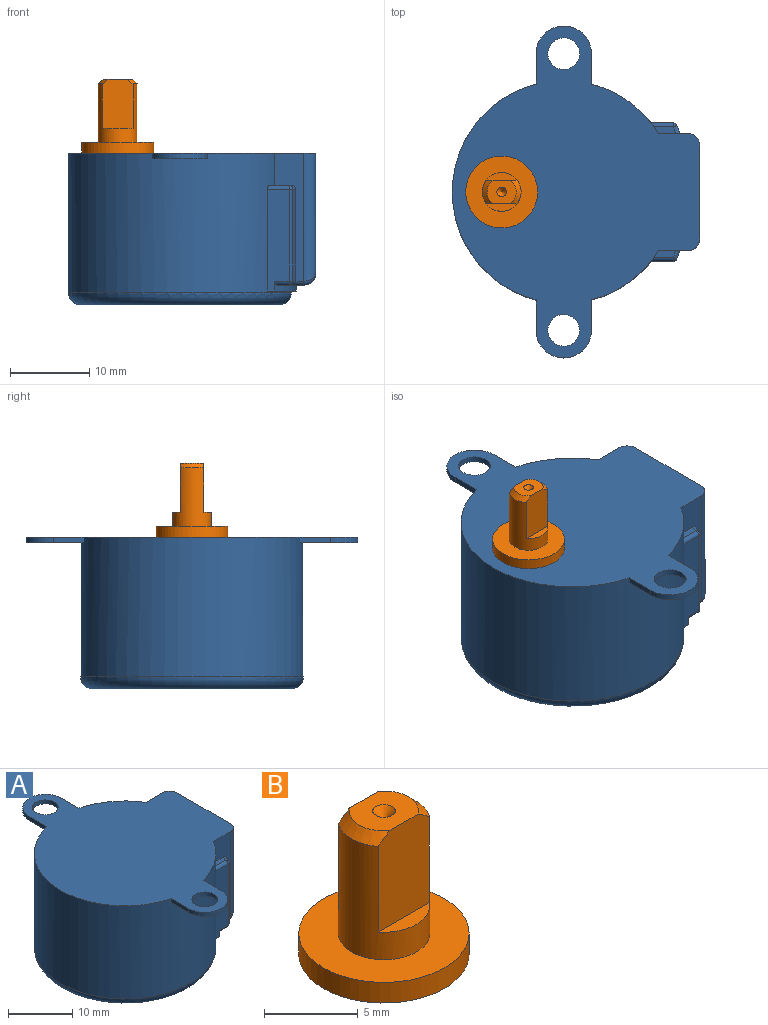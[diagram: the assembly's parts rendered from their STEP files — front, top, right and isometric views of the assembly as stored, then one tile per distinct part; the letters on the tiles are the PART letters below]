
ASSEMBLY  parts=2 mates=1
PART A: 53 faces, bbox 32.5x42x19.2 mm
  f0: plane 15.2x11.8mm, normal (1,0,0), area 169.8mm2, adj f14,f26,f27,f28,f48,f49,f50,f51
  f1: cylinder r=14.1mm len=28.2mm, axis (0,0,1), area 1250mm2, adj f2,f3,f4,f5,f6,f7,f8,f13
  f2: plane 16.5x4.27mm, normal (0,0,-1), area 30.7mm2, adj f1,f23,f24,f27,f34,f36,f37,f42
  f3: plane 16.2x3.7mm, normal (0,1,0), area 27.3mm2, adj f1,f14,f17,f18,f26,f30,f37
  f4: plane 3.84x0.75mm, normal (-1,0,0), area 2.9mm2, adj f1,f10,f13,f14
  f5: plane 3.84x0.75mm, normal (-1,0,0), area 2.9mm2, adj f1,f8,f9,f14
  f6: plane 3.84x0.75mm, normal (1,0,0), area 2.9mm2, adj f1,f10,f13,f14
  f7: plane 3.84x0.75mm, normal (1,0,0), area 2.9mm2, adj f1,f8,f9,f14
  f8: plane 7.34x7mm, normal (0,0,-1), area 31.5mm2, adj f1,f5,f7,f9,f12
  f9: cylinder r=3.5mm len=7mm, axis (0,0,1), area 8.2mm2, adj f5,f7,f8,f14
  f10: cylinder r=3.5mm len=7mm, axis (0,0,1), area 8.2mm2, adj f4,f6,f13,f14
  f11: cylinder r=2mm len=4mm, axis (0,0,1), area 9.4mm2, adj f13,f14
  f12: cylinder r=2mm len=4mm, axis (0,0,1), area 9.4mm2, adj f8,f14
  f13: plane 7.34x7mm, normal (0,0,-1), area 31.5mm2, adj f1,f4,f6,f10,f11
  f14: plane 42x31.3mm, normal (0,0,1), area 742.5mm2, adj f0,f1,f3,f4,f5,f6,f7,f9
  f15: plane 25.2x25.2mm, normal (0,0,-1), area 498.8mm2, adj f29
  f16: plane 16.2x3.7mm, normal (0,-1,0), area 27.3mm2, adj f1,f14,f20,f21,f28,f40,f46
  f17: plane 2.73x0.85mm, normal (0,0,1), area 1.9mm2, adj f1,f3,f30,f31
  f18: plane 11.6x1.02mm, normal (0.94,0.35,0), area 12.7mm2, adj f3,f30,f33,f36
  f19: plane 11.6x2.8mm, normal (0,1,0), area 32.4mm2, adj f1,f31,f33,f34
  f20: plane 2.73x0.85mm, normal (0,0,1), area 1.9mm2, adj f1,f16,f39,f40
  f21: plane 11.6x1.02mm, normal (0.94,-0.35,0), area 12.7mm2, adj f16,f40,f43,f45
  f22: plane 12.85x2.8mm, normal (0,-1,0), area 33.6mm2, adj f1,f23,f25,f39,f42,f43
  f23: cylinder r=14.85mm len=7.25mm, axis (0,0,1), area 6mm2, adj f2,f22,f24,f25,f42
  f24: plane 0.75x0.75mm, normal (0,1,0), area 0.6mm2, adj f1,f2,f23,f25
  f25: plane 7.25x3.71mm, normal (0,0,-1), area 5.9mm2, adj f1,f22,f23,f24
  f26: cylinder r=1.5mm len=16.2mm, axis (0,0,-1), area 37.3mm2, adj f0,f3,f14,f38
  f27: cylinder r=1.5mm len=13.8mm, axis (0,-1,0), area 30.8mm2, adj f0,f2,f38,f47
  f28: cylinder r=1.5mm len=16.2mm, axis (0,0,1), area 37.3mm2, adj f0,f14,f16,f47
  f29: torus R=12.6mm, axis (0,0,-1), area 200.7mm2, adj f1,f15
  f30: cylinder r=0.5mm len=1.2mm, axis (-0.35,0.94,0), area 0.8mm2, adj f3,f17,f18,f32
  f31: cylinder r=0.5mm len=2.8mm, axis (-1,0,0), area 2.1mm2, adj f1,f17,f19,f32
  f32: sphere r=0.5mm, area 0.3mm2, adj f30,f31,f33
  f33: cylinder r=0.5mm len=11.6mm, axis (0,0,-1), area 7.1mm2, adj f18,f19,f32,f35
  f34: cylinder r=0.5mm len=2.8mm, axis (-1,0,0), area 2.1mm2, adj f1,f2,f19,f35
  f35: sphere r=0.5mm, area 0.3mm2, adj f33,f34,f36
  f36: cylinder r=0.5mm len=1.52mm, axis (-0.35,0.94,0), area 1mm2, adj f2,f18,f35,f37
  f37: cylinder r=0.5mm len=1.35mm, axis (1,0,0), area 0.9mm2, adj f2,f3,f36,f38
  f38: bspline ~1.76x1.5mm, area 1.3mm2, adj f26,f27,f37
  f39: cylinder r=0.5mm len=2.8mm, axis (1,0,0), area 2.1mm2, adj f1,f20,f22,f41
  f40: cylinder r=0.5mm len=1.2mm, axis (0.35,0.94,0), area 0.8mm2, adj f16,f20,f21,f41
  f41: sphere r=0.5mm, area 0.3mm2, adj f39,f40,f43
  f42: cylinder r=0.5mm len=1.86mm, axis (1,0,0), area 1.4mm2, adj f2,f22,f23,f44
  f43: cylinder r=0.5mm len=11.6mm, axis (0,0,-1), area 7.1mm2, adj f21,f22,f41,f44
  f44: sphere r=0.5mm, area 0.3mm2, adj f42,f43,f45
  f45: cylinder r=0.5mm len=1.52mm, axis (0.35,0.94,0), area 1mm2, adj f2,f21,f44,f46
  f46: cylinder r=0.5mm len=1.35mm, axis (-1,0,0), area 0.9mm2, adj f2,f16,f45,f47
  f47: bspline ~1.76x1.5mm, area 1.3mm2, adj f27,f28,f46
  f48: plane 6.3x1mm, normal (0,0,1), area 6.3mm2, adj f0,f49,f51,f52
  f49: cylinder r=0.65mm len=1.3mm, axis (1,0,0), area 2mm2, adj f0,f48,f50,f52
  f50: plane 6.3x1mm, normal (0,0,-1), area 6.3mm2, adj f0,f49,f51,f52
  f51: cylinder r=0.65mm len=1.3mm, axis (1,0,0), area 2mm2, adj f0,f48,f50,f52
  f52: plane 7.6x1.3mm, normal (1,0,0), area 9.5mm2, adj f48,f49,f50,f51
PART B: 12 faces, bbox 9.2x9.2x9.5 mm
  f0: cylinder r=2.45mm len=7.4mm, axis (0,0,-1), area 63.9mm2, adj f1,f2,f4,f8,f9,f10,f11
  f1: cone r=1.85mm half-angle=45deg, axis (0,0,-1), area 2.9mm2, adj f0,f3,f9,f11
  f2: cone r=1.85mm half-angle=45deg, axis (0,0,-1), area 2.9mm2, adj f0,f3,f9,f11
  f3: plane 3.7x3mm, normal (0,0,1), area 8.6mm2, adj f1,f2,f5,f9,f11
  f4: plane 9.1x9.1mm, normal (0,0,1), area 46.2mm2, adj f0,f7
  f5: cone r=0.6mm half-angle=45deg, axis (0,0,1), area 1.6mm2, adj f3
  f6: plane 9.1x9.1mm, normal (0,0,-1), area 65mm2, adj f7
  f7: cylinder r=4.55mm len=9.1mm, axis (0,0,-1), area 38.6mm2, adj f4,f6
  f8: plane 3.87x0.95mm, normal (0,0,1), area 2.6mm2, adj f0,f9
  f9: plane 6.31x3.98mm, normal (0,-1,0), area 23.5mm2, adj f0,f1,f2,f3,f8
  f10: plane 3.87x0.95mm, normal (0,0,1), area 2.6mm2, adj f0,f11
  f11: plane 6.31x3.98mm, normal (0,1,0), area 23.5mm2, adj f0,f1,f2,f3,f10
PLACE A t=(-8.98,0,0)mm
PLACE B t=(-8.98,0,0)mm
MATE fastened A.f1 <-> B.f6  axis (0,0,1) through (-1.13,0,0)mm
